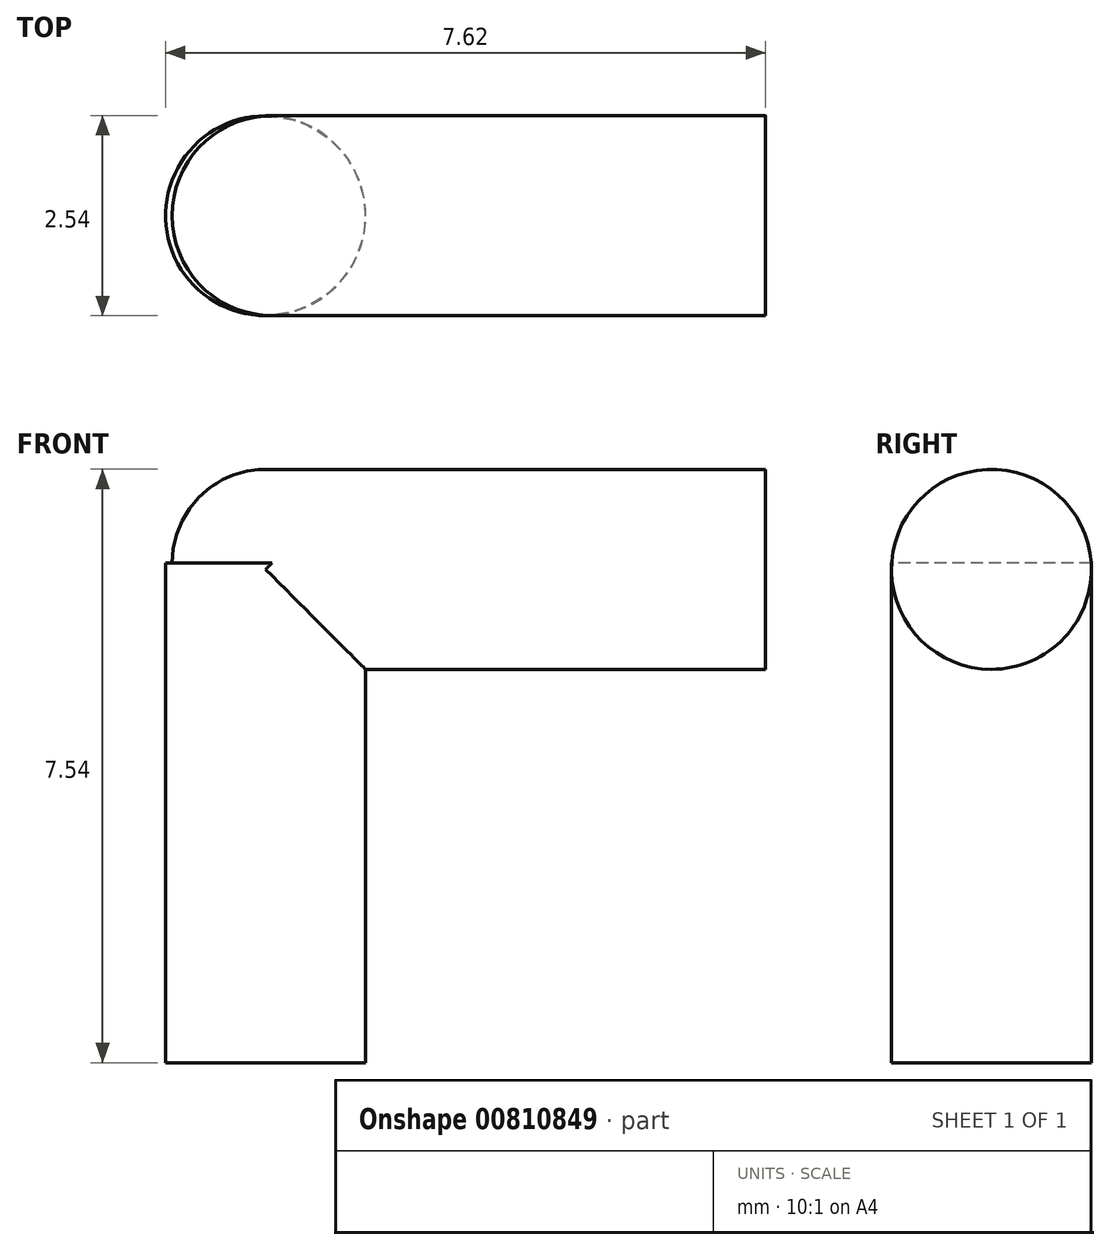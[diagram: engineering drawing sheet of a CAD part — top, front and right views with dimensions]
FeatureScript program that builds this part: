
annotation { "Feature Type Name" : "Feature", "Feature Type Description" : "" }
export const myFeature = defineFeature(function(context is Context, id is Id, definition is map)
    precondition{}
    {
        {
            var Q0;
            Q0=qCreatedBy(makeId("Top.planeOp"),FACE);
            var sketch = newSketch(context, id + "F0", { "sketchPlane" : qUnion([Q0])});
            skCircle(sketch, "E0", {"center": v(0, 0) * mm, "radius": 1.27 * mm});
            skSolve(sketch);
        }
        {
            var Q0;
            Q0 = qSketchRegion(id + "F0", true);
            extrude(context, id + "F1", {"entities" : qUnion([Q0]), "depth" : 6.35 * mm, "offsetDistance" : 25.4 * mm});
        }
        {
            var Q0;
            Q0=qCreatedBy(makeId("Right.planeOp"),FACE);
            var sketch = newSketch(context, id + "F2", { "sketchPlane" : qUnion([Q0])});
            skCircle(sketch, "E1", {"center": v(0, 6.27) * mm, "radius": 1.27 * mm});
            skSolve(sketch);
        }
        {
            var Q0;
            Q0 = qSketchRegion(id + "F2", true);
            extrude(context, id + "F3", {"entities" : qUnion([Q0]), "operationType" : NewBodyOperationType.ADD, "depth" : 6.35 * mm, "offsetDistance" : 25.4 * mm});
        }
        {
            var Q0;
            Q0=makeQuery(id+"F3.opExtrude","CAP_FACE",FACE,{"disambiguationData":[OSD([sQuery(id+"F2.wireOp",EDGE,"E1")])],"isStart":true});
            var sketch = newSketch(context, id + "F4", { "sketchPlane" : qUnion([Q0])});
            skArc(sketch, "E2.0", {"start": v(-1.27, 6.35) * mm, "mid": v(0, 7.54) * mm, "end": v(1.27, 6.35) * mm});
            skLineSegment(sketch, "E2.1", {"start": v(1.27, 6.35) * mm, "end": v(-1.27, 6.35) * mm});
            skSolve(sketch);
        }
        {
            var Q0;
            Q0=makeQuery(id+"F4.imprint","IMPRINT",FACE,{"disambiguationData":[TD([[makeQuery(id+"F4.imprint","IMPRINT",EDGE,{"derivedFrom":sQuery(id+"F4.wireOp",EDGE,"E2.0")}),-1.0]])]});
            var Q1;
            Q1=sQuery(id+"F4.wireOp",EDGE,"E2.1");
            revolve(context, id + "F5", {"operationType" : NewBodyOperationType.ADD, "surfaceOperationType" : NewSurfaceOperationType.NEW, "entities" : qUnion([Q0]), "axis" : qUnion([Q1]), "revolveType" : RevolveType.FULL});
        }
        {
            var Q0;
            Q0 = qSketchRegion(id + "F4", true);
            var Q1;
            Q1=sQuery(id+"F4.wireOp",EDGE,"E2.1");
            revolve(context, id + "F6", {"operationType" : NewBodyOperationType.ADD, "surfaceOperationType" : NewSurfaceOperationType.NEW, "entities" : qUnion([Q0]), "axis" : qUnion([Q1]), "revolveType" : RevolveType.FULL});
        }
    });
